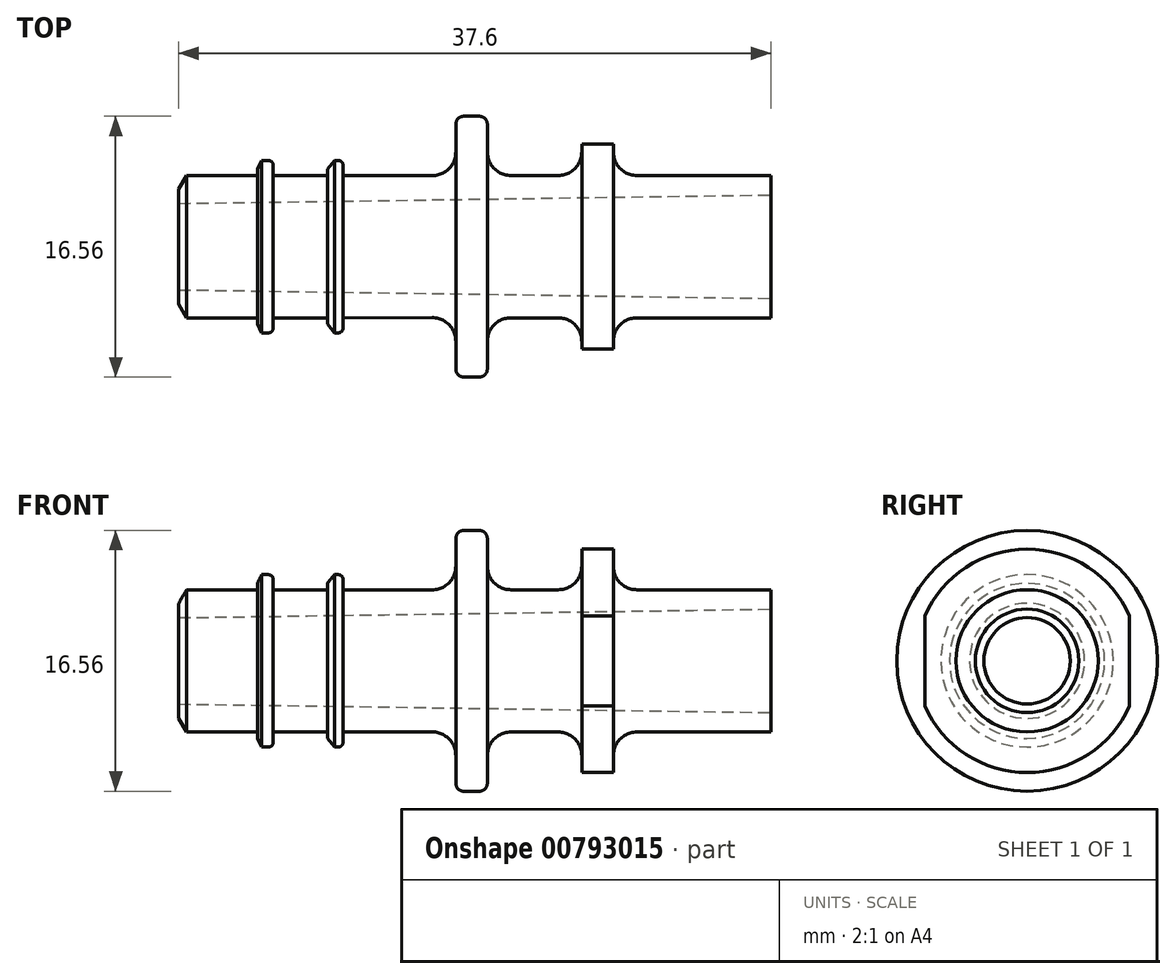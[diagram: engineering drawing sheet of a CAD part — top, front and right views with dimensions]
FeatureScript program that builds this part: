
annotation { "Feature Type Name" : "Feature", "Feature Type Description" : "" }
export const myFeature = defineFeature(function(context is Context, id is Id, definition is map)
    precondition{}
    {
        {
            var Q0;
            Q0=qCreatedBy(makeId("Front.planeOp"),FACE);
            var sketch = newSketch(context, id + "F0", { "sketchPlane" : qUnion([Q0])});
            skLineSegment(sketch, "E0", {"start": v(-15.46, 4.52) * mm, "end": v(-10.96, 4.52) * mm});
            skLineSegment(sketch, "E1", {"start": v(-9.96, 4.52) * mm, "end": v(-6.52, 4.52) * mm});
            skLineSegment(sketch, "E2", {"start": v(3.64, 7.78) * mm, "end": v(3.64, 6.02) * mm});
            skLineSegment(sketch, "E3", {"start": v(5.14, 4.52) * mm, "end": v(8.14, 4.52) * mm});
            skLineSegment(sketch, "E4", {"start": v(9.64, 6.02) * mm, "end": v(9.64, 7.1) * mm});
            skLineSegment(sketch, "E5", {"start": v(11.64, 7.1) * mm, "end": v(11.64, 6.02) * mm});
            skLineSegment(sketch, "E6", {"start": v(13.14, 4.52) * mm, "end": v(21.64, 4.52) * mm});
            skLineSegment(sketch, "E7", {"start": v(21.64, 4.52) * mm, "end": v(21.64, 3.28) * mm});
            skLineSegment(sketch, "E8", {"start": v(-15.96, 3.65) * mm, "end": v(-15.96, 2.74) * mm});
            skPoint(sketch, "E9.end.orphan", {"position": v(-10.17, 4.92) * mm});
            skPoint(sketch, "E10.end.orphan", {"position": v(-6.52, 4.92) * mm});
            skLineSegment(sketch, "E11", {"start": v(-5.52, 4.52) * mm, "end": v(-5.52, 5.17) * mm});
            skLineSegment(sketch, "E12", {"start": v(-5.82, 5.47) * mm, "end": v(-6.07, 5.47) * mm});
            skLineSegment(sketch, "E13", {"start": v(-6.07, 5.47) * mm, "end": v(-6.52, 4.92) * mm});
            skLineSegment(sketch, "E14", {"start": v(-6.52, 4.92) * mm, "end": v(-6.52, 4.52) * mm});
            skPoint(sketch, "E15.start.orphan", {"position": v(3.66, 8.17) * mm});
            skLineSegment(sketch, "E16", {"start": v(3.14, 8.28) * mm, "end": v(2.14, 8.28) * mm});
            skLineSegment(sketch, "E17", {"start": v(1.64, 7.78) * mm, "end": v(1.64, 6) * mm});
            skPoint(sketch, "E18.end.orphan", {"position": v(0, 4.12) * mm});
            skLineSegment(sketch, "E19", {"start": v(-5.52, 4.52) * mm, "end": v(0.13, 4.5) * mm});
            skPoint(sketch, "E20.end.orphan", {"position": v(-10.96, 5.47) * mm});
            skLineSegment(sketch, "E21", {"start": v(-9.96, 4.52) * mm, "end": v(-9.96, 5.17) * mm});
            skLineSegment(sketch, "E22", {"start": v(-10.26, 5.47) * mm, "end": v(-10.7, 5.47) * mm});
            skLineSegment(sketch, "E23", {"start": v(-10.7, 5.47) * mm, "end": v(-10.96, 4.92) * mm});
            skLineSegment(sketch, "E24", {"start": v(-10.96, 4.92) * mm, "end": v(-10.96, 4.52) * mm});
            skPoint(sketch, "E25.visualSharp", {"position": v(1.64, 8.28) * mm});
            skArc(sketch, "E25.filletArc", {"start": v(2.14, 8.28) * mm, "mid": v(1.78, 8.13) * mm, "end": v(1.64, 7.78) * mm});
            skPoint(sketch, "E26.visualSharp", {"position": v(3.64, 8.28) * mm});
            skArc(sketch, "E26.filletArc", {"start": v(3.64, 7.78) * mm, "mid": v(3.5, 8.13) * mm, "end": v(3.14, 8.28) * mm});
            skPoint(sketch, "E27.visualSharp", {"position": v(3.64, 4.52) * mm});
            skArc(sketch, "E27.filletArc", {"start": v(3.64, 6.02) * mm, "mid": v(4.08, 4.96) * mm, "end": v(5.14, 4.52) * mm});
            skPoint(sketch, "E28.visualSharp", {"position": v(9.64, 4.52) * mm});
            skArc(sketch, "E28.filletArc", {"start": v(8.14, 4.52) * mm, "mid": v(9.2, 4.96) * mm, "end": v(9.64, 6.02) * mm});
            skPoint(sketch, "E29.visualSharp", {"position": v(1.64, 4.5) * mm});
            skArc(sketch, "E29.filletArc", {"start": v(0.13, 4.5) * mm, "mid": v(1.2, 4.95) * mm, "end": v(1.64, 6) * mm});
            skPoint(sketch, "E30.visualSharp", {"position": v(11.64, 4.52) * mm});
            skArc(sketch, "E30.filletArc", {"start": v(11.64, 6.02) * mm, "mid": v(12.08, 4.96) * mm, "end": v(13.14, 4.52) * mm});
            skPoint(sketch, "E31.visualSharp", {"position": v(-5.52, 5.47) * mm});
            skArc(sketch, "E31.filletArc", {"start": v(-5.52, 5.17) * mm, "mid": v(-5.61, 5.39) * mm, "end": v(-5.82, 5.47) * mm});
            skPoint(sketch, "E32.visualSharp", {"position": v(-9.96, 5.47) * mm});
            skArc(sketch, "E32.filletArc", {"start": v(-9.96, 5.17) * mm, "mid": v(-10.05, 5.39) * mm, "end": v(-10.26, 5.47) * mm});
            skLineSegment(sketch, "E33", {"start": v(-15.46, 4.52) * mm, "end": v(-15.46, 2.75) * mm});
            skLineSegment(sketch, "E34", {"start": v(-15.46, 4.52) * mm, "end": v(-15.96, 3.65) * mm});
            skLineSegment(sketch, "E35", {"start": v(9.64, 7.1) * mm, "end": v(11.64, 7.1) * mm});
            skPoint(sketch, "E36.orphan", {"position": v(11.64, 8.17) * mm});
            skPoint(sketch, "E37.orphan", {"position": v(9.64, 8.17) * mm});
            skLineSegment(sketch, "E38", {"start": v(21.64, 3.28) * mm, "end": v(-15.96, 2.74) * mm});
            skPoint(sketch, "E39.orphan", {"position": v(-15.46, 0) * mm});
            skPoint(sketch, "E40.orphan", {"position": v(-15.96, 0) * mm});
            skPoint(sketch, "E41.orphan", {"position": v(21.64, 0) * mm});
            skLineSegment(sketch, "E42", {"start": v(21.64, 3.28) * mm, "end": v(21.64, 0) * mm});
            skLineSegment(sketch, "E43", {"start": v(-15.96, 2.74) * mm, "end": v(-15.96, 0) * mm});
            skLineSegment(sketch, "E44", {"start": v(-15.96, 0) * mm, "end": v(21.64, 0) * mm});
            skSolve(sketch);
        }
        {
            var Q0;
            {var subQ0=sQuery(id+"F0.wireOp",EDGE,"E8");Q0=makeQuery(id+"F0.imprint","IMPRINT",FACE,{"disambiguationData":[TD([[makeQuery(id+"F0.imprint","IMPRINT",EDGE,{"derivedFrom":subQ0}),1.0]])]});}
            var Q1;
            Q1=makeQuery(id+"F0.imprint","IMPRINT",FACE,{"disambiguationData":[TD([[makeQuery(id+"F0.imprint","IMPRINT",EDGE,{"derivedFrom":sQuery(id+"F0.wireOp",EDGE,"E0")}),-1.0]])]});
            var Q2;
            Q2=sQuery(id+"F0.wireOp",EDGE,"E44");
            revolve(context, id + "F1", {"surfaceOperationType" : NewSurfaceOperationType.NEW, "entities" : qUnion([Q0, Q1]), "axis" : qUnion([Q2]), "revolveType" : RevolveType.FULL});
        }
        {
            var Q0;
            Q0=makeQuery(id+"F1.opRevolve","SWEPT_FACE",FACE,{"disambiguationData":[OSD([sQuery(id+"F0.wireOp",EDGE,"E5")])]});
            var sketch = newSketch(context, id + "F2", { "sketchPlane" : qUnion([Q0])});
            skLineSegment(sketch, "E45", {"start": v(-6.5, 2.85) * mm, "end": v(-6.5, -2.85) * mm});
            skLineSegment(sketch, "E46", {"start": v(6.5, 2.85) * mm, "end": v(6.5, -2.85) * mm});
            skSolve(sketch);
        }
        {
            var Q0;
            {var subQ0=sQuery(id+"F2.wireOp",EDGE,"E45");Q0=makeQuery(id+"F2.imprint","IMPRINT",FACE,{"disambiguationData":[TD([[makeQuery(id+"F2.imprint","IMPRINT",EDGE,{"derivedFrom":subQ0}),-1.0]])]});}
            var Q1;
            {var subQ0=sQuery(id+"F2.wireOp",EDGE,"E46");Q1=makeQuery(id+"F2.imprint","IMPRINT",FACE,{"disambiguationData":[TD([[makeQuery(id+"F2.imprint","IMPRINT",EDGE,{"derivedFrom":subQ0}),1.0]])]});}
            extrude(context, id + "F3", {"entities" : qUnion([Q0, Q1]), "operationType" : NewBodyOperationType.REMOVE, "oppositeDirection" : true, "depth" : 4 * mm, "offsetDistance" : 25 * mm});
        }
    });
